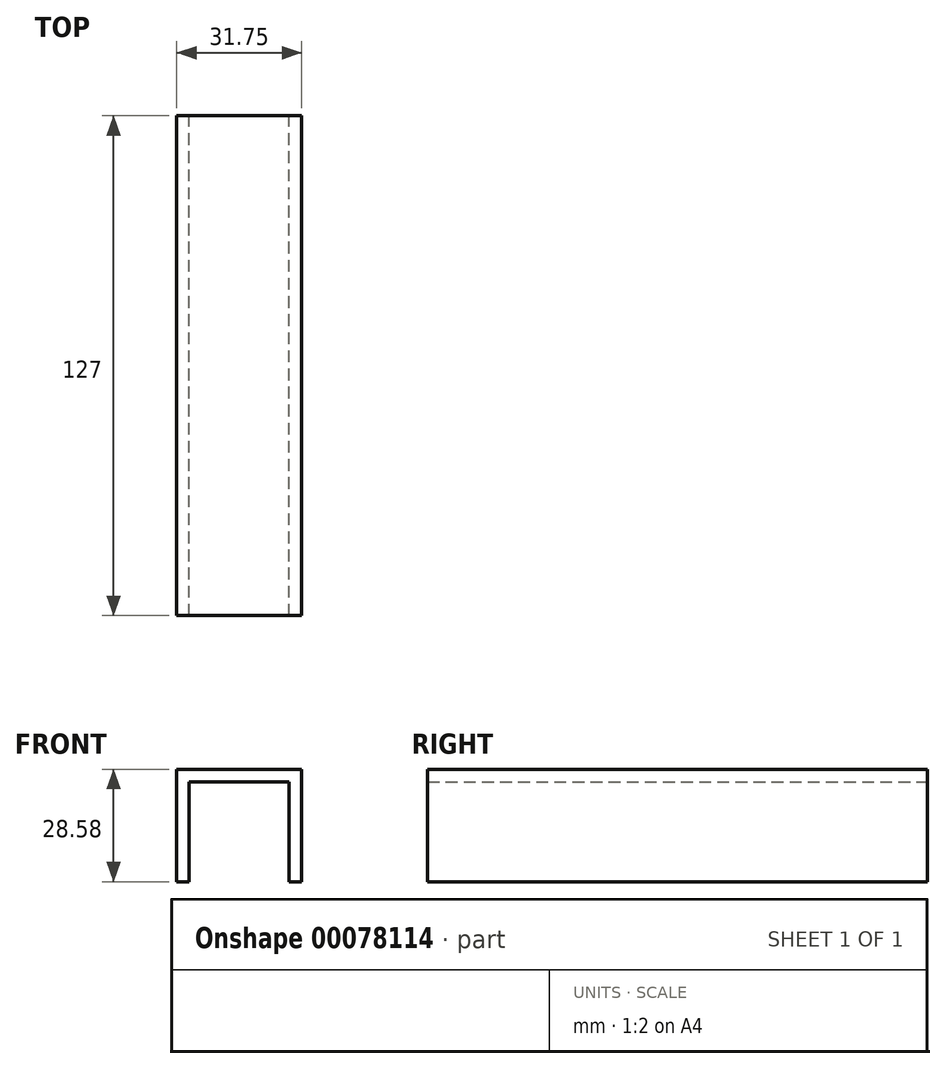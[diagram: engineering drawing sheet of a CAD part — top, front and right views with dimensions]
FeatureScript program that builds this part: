
annotation { "Feature Type Name" : "Feature", "Feature Type Description" : "" }
export const myFeature = defineFeature(function(context is Context, id is Id, definition is map)
    precondition{}
    {
        {
            var Q0;
            Q0=qCreatedBy(makeId("Front.planeOp"),FACE);
            var sketch = newSketch(context, id + "F0", { "sketchPlane" : qUnion([Q0])});
            skLineSegment(sketch, "E0.bottom", {"start": v(-44.8, 16.94) * mm, "end": v(-19.4, 16.94) * mm});
            skLineSegment(sketch, "E0.top", {"start": v(-44.8, 13.76) * mm, "end": v(-19.4, 13.76) * mm});
            skLineSegment(sketch, "E0.left", {"start": v(-44.8, 16.94) * mm, "end": v(-44.8, 13.76) * mm});
            skLineSegment(sketch, "E0.right", {"start": v(-19.4, 16.94) * mm, "end": v(-19.4, 13.76) * mm});
            skLineSegment(sketch, "E1.bottom", {"start": v(-44.8, 16.94) * mm, "end": v(-47.97, 16.94) * mm});
            skLineSegment(sketch, "E1.top", {"start": v(-44.8, -11.64) * mm, "end": v(-47.97, -11.64) * mm});
            skLineSegment(sketch, "E1.left", {"start": v(-44.8, 16.94) * mm, "end": v(-44.8, -11.64) * mm});
            skLineSegment(sketch, "E1.right", {"start": v(-47.97, 16.94) * mm, "end": v(-47.97, -11.64) * mm});
            skLineSegment(sketch, "E2.bottom", {"start": v(-19.4, 16.94) * mm, "end": v(-16.22, 16.94) * mm});
            skLineSegment(sketch, "E2.top", {"start": v(-19.4, -11.64) * mm, "end": v(-16.22, -11.64) * mm});
            skLineSegment(sketch, "E2.left", {"start": v(-19.4, 16.94) * mm, "end": v(-19.4, -11.64) * mm});
            skLineSegment(sketch, "E2.right", {"start": v(-16.22, 16.94) * mm, "end": v(-16.22, -11.64) * mm});
            skSolve(sketch);
        }
        {
            var Q0;
            Q0 = qSketchRegion(id + "F0", true);
            extrude(context, id + "F1", {"entities" : qUnion([Q0]), "depth" : 127 * mm});
        }
    });
